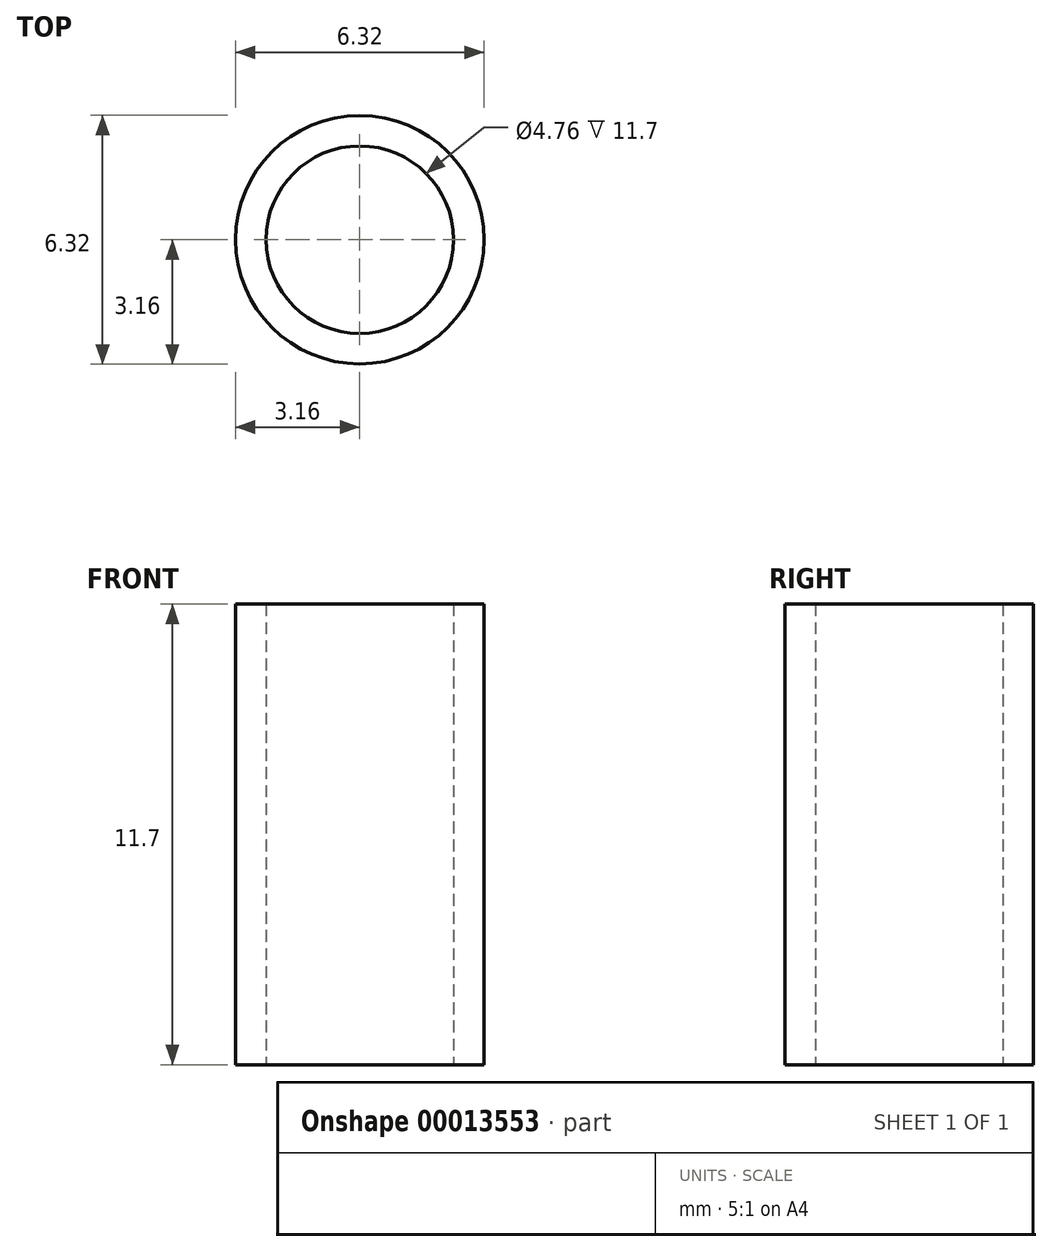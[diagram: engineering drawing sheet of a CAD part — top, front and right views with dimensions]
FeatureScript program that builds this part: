
annotation { "Feature Type Name" : "Feature", "Feature Type Description" : "" }
export const myFeature = defineFeature(function(context is Context, id is Id, definition is map)
    precondition{}
    {
        {
            var Q0;
            Q0=qCreatedBy(makeId("Top.planeOp"),FACE);
            var sketch = newSketch(context, id + "F0", { "sketchPlane" : qUnion([Q0])});
            skCircle(sketch, "E0", {"center": v(0, 0) * mm, "radius": 2.38 * mm});
            skCircle(sketch, "E1", {"center": v(0, 0) * mm, "radius": 3.16 * mm});
            skSolve(sketch);
        }
        {
            var Q0;
            Q0 = qSketchRegion(id + "F0", true);
            extrude(context, id + "F1", {"entities" : qUnion([Q0]), "depth" : 11.7 * mm});
        }
    });
